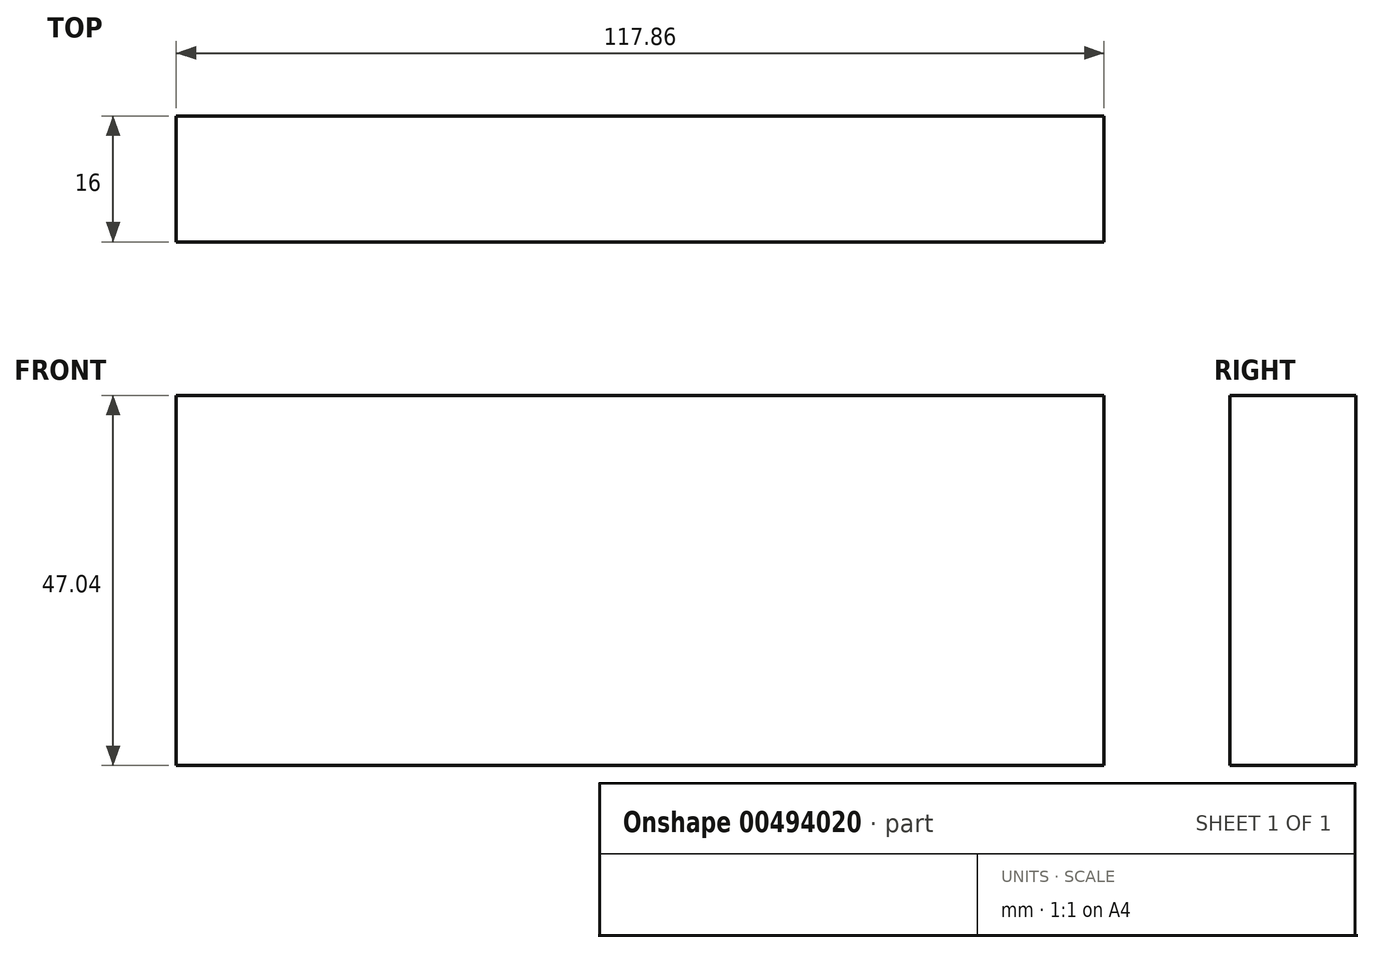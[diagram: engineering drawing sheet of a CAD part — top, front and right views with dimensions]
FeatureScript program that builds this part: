
annotation { "Feature Type Name" : "Feature", "Feature Type Description" : "" }
export const myFeature = defineFeature(function(context is Context, id is Id, definition is map)
    precondition{}
    {
        {
            var Q0;
            Q0=qCreatedBy(makeId("Front.planeOp"),FACE);
            var sketch = newSketch(context, id + "F0", { "sketchPlane" : qUnion([Q0])});
            skLineSegment(sketch, "E0.bottom", {"start": v(-58.93, 23.52) * mm, "end": v(58.93, 23.52) * mm});
            skLineSegment(sketch, "E0.top", {"start": v(-58.93, -23.52) * mm, "end": v(58.93, -23.52) * mm});
            skLineSegment(sketch, "E0.left", {"start": v(-58.93, 23.52) * mm, "end": v(-58.93, -23.52) * mm});
            skLineSegment(sketch, "E0.right", {"start": v(58.93, 23.52) * mm, "end": v(58.93, -23.52) * mm});
            skPoint(sketch, "E0.middle", {"position": v(0, 0) * mm});
            skSolve(sketch);
        }
        {
            var Q0;
            Q0=makeQuery(id+"F0.imprint","IMPRINT",FACE,{"disambiguationData":[TD([[makeQuery(id+"F0.imprint","IMPRINT",EDGE,{"derivedFrom":sQuery(id+"F0.wireOp",EDGE,"E0.bottom")}),-1.0]])]});
            extrude(context, id + "F1", {"entities" : qUnion([Q0]), "depth" : 16 * mm});
        }
    });
